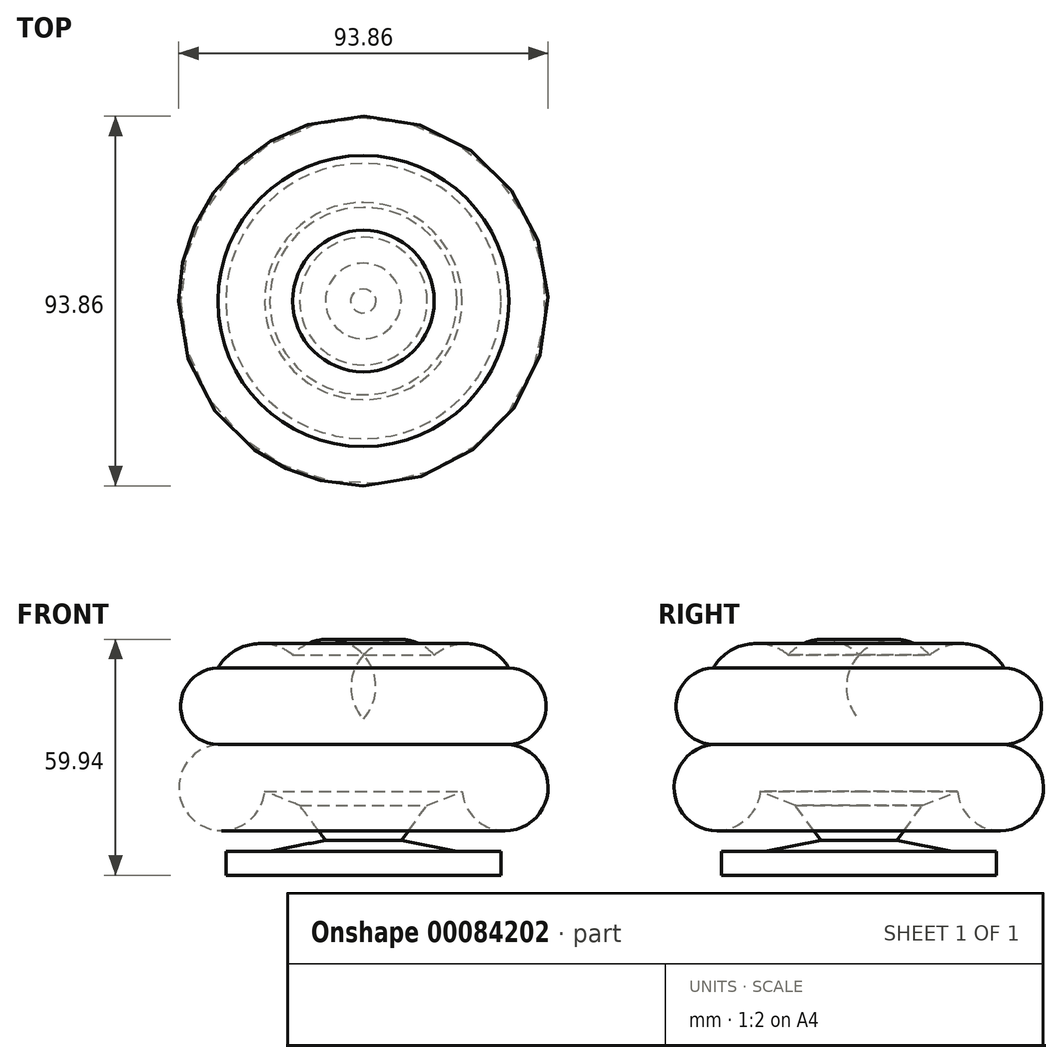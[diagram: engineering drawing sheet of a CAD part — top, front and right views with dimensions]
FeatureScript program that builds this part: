
annotation { "Feature Type Name" : "Feature", "Feature Type Description" : "" }
export const myFeature = defineFeature(function(context is Context, id is Id, definition is map)
    precondition{}
    {
        {
            var Q0;
            Q0=qCreatedBy(makeId("Front.planeOp"),FACE);
            var sketch = newSketch(context, id + "F0", { "sketchPlane" : qUnion([Q0])});
            skLineSegment(sketch, "E0", {"start": v(0, 0) * mm, "end": v(0, 55.96) * mm});
            skArc(sketch, "E1", {"start": v(17.98, 55.96) * mm, "mid": v(8.99, 59.94) * mm, "end": v(0, 55.96) * mm});
            skArc(sketch, "E2", {"start": v(36.97, 52.66) * mm, "mid": v(28.23, 58.68) * mm, "end": v(17.98, 55.96) * mm});
            skArc(sketch, "E3", {"start": v(36.97, 33.17) * mm, "mid": v(46.45, 42.92) * mm, "end": v(36.97, 52.66) * mm});
            skArc(sketch, "E4", {"start": v(25.07, 21.27) * mm, "mid": v(43.72, 14.51) * mm, "end": v(36.97, 33.17) * mm});
            skLineSegment(sketch, "E5", {"start": v(25.07, 21.27) * mm, "end": v(16.2, 17.72) * mm});
            skLineSegment(sketch, "E6", {"start": v(16.2, 17.72) * mm, "end": v(9.62, 8.86) * mm});
            skLineSegment(sketch, "E7", {"start": v(9.62, 8.86) * mm, "end": v(23.8, 6.08) * mm});
            skLineSegment(sketch, "E8", {"start": v(23.8, 6.08) * mm, "end": v(34.94, 6.08) * mm});
            skLineSegment(sketch, "E9", {"start": v(34.94, 6.08) * mm, "end": v(34.94, 0) * mm});
            skLineSegment(sketch, "E10", {"start": v(34.94, 0) * mm, "end": v(0, 0) * mm});
            skSolve(sketch);
        }
        {
            var Q0;
            Q0=makeQuery(id+"F0.imprint","IMPRINT",FACE,{"disambiguationData":[TD([[makeQuery(id+"F0.imprint","IMPRINT",EDGE,{"derivedFrom":sQuery(id+"F0.wireOp",EDGE,"E0")}),-1.0]])]});
            var Q1;
            Q1=sQuery(id+"F0.wireOp",EDGE,"E0");
            revolve(context, id + "F1", {"entities" : qUnion([Q0]), "axis" : qUnion([Q1]), "revolveType" : RevolveType.FULL});
        }
        {
            var Q0;
            Q0=qCreatedBy(makeId("Front.planeOp"),FACE);
            var sketch = newSketch(context, id + "F2", { "sketchPlane" : qUnion([Q0])});
            skLineSegment(sketch, "E11", {"start": v(0, -38.35) * mm, "end": v(0, -7) * mm});
            skLineSegment(sketch, "E12", {"start": v(0, -7) * mm, "end": v(15.18, -7) * mm});
            skLineSegment(sketch, "E13", {"start": v(15.18, -7) * mm, "end": v(15.18, -38.78) * mm});
            skLineSegment(sketch, "E14", {"start": v(15.18, -38.78) * mm, "end": v(34.5, -38.78) * mm});
            skLineSegment(sketch, "E15", {"start": v(34.5, -38.78) * mm, "end": v(34.5, -67.97) * mm});
            skLineSegment(sketch, "E16", {"start": v(34.5, -67.97) * mm, "end": v(-20.88, -67.97) * mm});
            skLineSegment(sketch, "E17", {"start": v(-20.88, -67.97) * mm, "end": v(-20.88, -41.35) * mm});
            skLineSegment(sketch, "E18", {"start": v(-20.88, -41.35) * mm, "end": v(0, -38.35) * mm});
            skSolve(sketch);
        }
        {
            var Q0;
            Q0 = qSketchRegion(id + "F2", true);
            extrude(context, id + "F3", {"entities" : qUnion([Q0]), "operationType" : NewBodyOperationType.REMOVE, "oppositeDirection" : true, "depth" : 25.4 * mm});
        }
    });
